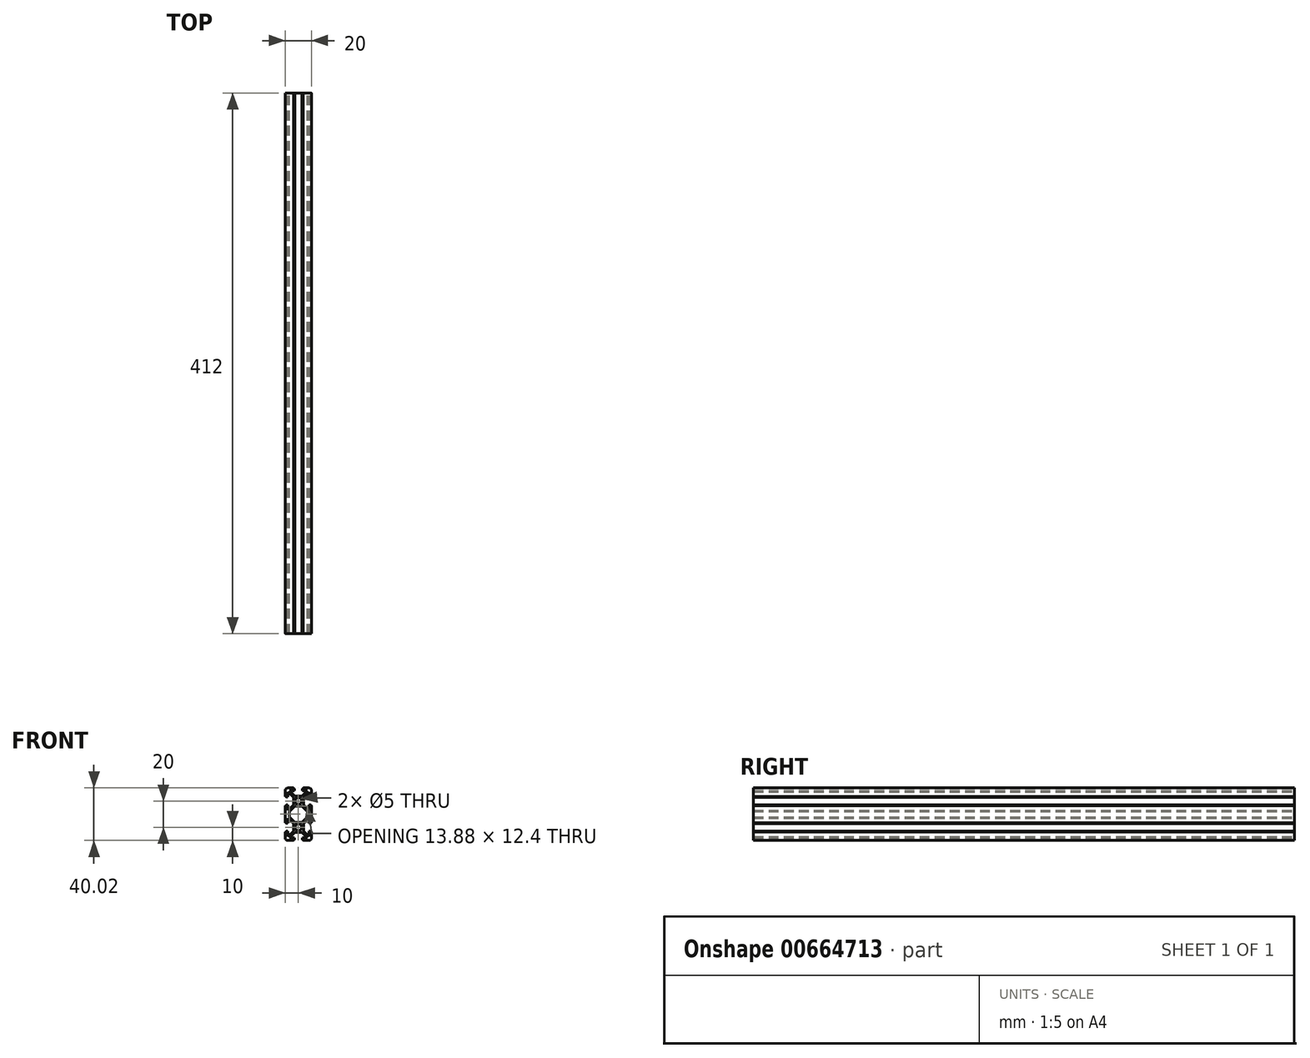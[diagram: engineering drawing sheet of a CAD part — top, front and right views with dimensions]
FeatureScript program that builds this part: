
annotation { "Feature Type Name" : "Feature", "Feature Type Description" : "" }
export const myFeature = defineFeature(function(context is Context, id is Id, definition is map)
    precondition{}
    {
        {
            var Q0;
            Q0=qCreatedBy(makeId("Front.planeOp"),FACE);
            var sketch = newSketch(context, id + "F0", { "sketchPlane" : qUnion([Q0])});
            skPoint(sketch, "E0.middle", {"position": v(10, -10) * mm});
            skPoint(sketch, "E1.visualSharp", {"position": v(0, 0) * mm});
            skArc(sketch, "E1.filletArc", {"start": v(2, 0) * mm, "mid": v(0.59, -0.59) * mm, "end": v(0, -2) * mm});
            skPoint(sketch, "E2.visualSharp", {"position": v(20, 0) * mm});
            skArc(sketch, "E2.filletArc", {"start": v(20, -2) * mm, "mid": v(19.41, -0.59) * mm, "end": v(18, 0) * mm});
            skPoint(sketch, "E3.visualSharp", {"position": v(20, -20) * mm});
            skLineSegment(sketch, "E4", {"start": v(2, 0) * mm, "end": v(6.5, 0) * mm});
            skLineSegment(sketch, "E5", {"start": v(6.5, 0) * mm, "end": v(6.5, -0.5) * mm});
            skLineSegment(sketch, "E6", {"start": v(13.02, -0.5) * mm, "end": v(13.5, -0.5) * mm});
            skLineSegment(sketch, "E7", {"start": v(13.5, 0.02) * mm, "end": v(18, 0) * mm});
            skLineSegment(sketch, "E8", {"start": v(20, -2) * mm, "end": v(20, -6.5) * mm});
            skLineSegment(sketch, "E9", {"start": v(20, -6.5) * mm, "end": v(19.5, -6.5) * mm});
            skLineSegment(sketch, "E10", {"start": v(19.5, -6.5) * mm, "end": v(19.5, -7) * mm});
            skLineSegment(sketch, "E11", {"start": v(13.83, -7.25) * mm, "end": v(13.83, -12.77) * mm});
            skLineSegment(sketch, "E12", {"start": v(19.53, -12.98) * mm, "end": v(19.54, -13.46) * mm});
            skLineSegment(sketch, "E13", {"start": v(12.74, -13.8) * mm, "end": v(7.26, -13.8) * mm});
            skLineSegment(sketch, "E14", {"start": v(6.2, -12.74) * mm, "end": v(6.2, -7.26) * mm});
            skLineSegment(sketch, "E15", {"start": v(0, -6.49) * mm, "end": v(0, -2) * mm});
            skLineSegment(sketch, "E16", {"start": v(7, -0.5) * mm, "end": v(7, -2) * mm});
            skLineSegment(sketch, "E17", {"start": v(7, -2) * mm, "end": v(3.06, -2) * mm});
            skLineSegment(sketch, "E18", {"start": v(3.06, -2) * mm, "end": v(7.26, -6.2) * mm});
            skLineSegment(sketch, "E19", {"start": v(12.74, -6.2) * mm, "end": v(16.94, -2) * mm});
            skLineSegment(sketch, "E20", {"start": v(16.94, -2) * mm, "end": v(13.02, -2) * mm});
            skLineSegment(sketch, "E21", {"start": v(19.53, -12.98) * mm, "end": v(18, -12.98) * mm});
            skLineSegment(sketch, "E22", {"start": v(18, -12.98) * mm, "end": v(18, -16.94) * mm});
            skLineSegment(sketch, "E23", {"start": v(18, -16.94) * mm, "end": v(13.83, -12.77) * mm});
            skLineSegment(sketch, "E24", {"start": v(13.83, -7.25) * mm, "end": v(18, -3.06) * mm});
            skLineSegment(sketch, "E25", {"start": v(18, -3.06) * mm, "end": v(18, -7) * mm});
            skLineSegment(sketch, "E26", {"start": v(18, -7) * mm, "end": v(19.5, -7) * mm});
            skLineSegment(sketch, "E27", {"start": v(16.94, -18) * mm, "end": v(12.74, -13.8) * mm});
            skLineSegment(sketch, "E28", {"start": v(7.26, -13.8) * mm, "end": v(3.06, -18) * mm});
            skLineSegment(sketch, "E29", {"start": v(0.5, -6.49) * mm, "end": v(0.5, -7) * mm});
            skLineSegment(sketch, "E30", {"start": v(0.5, -7) * mm, "end": v(2, -7) * mm});
            skLineSegment(sketch, "E31", {"start": v(2, -7) * mm, "end": v(2, -3.08) * mm});
            skLineSegment(sketch, "E32", {"start": v(2, -3.08) * mm, "end": v(6.2, -7.26) * mm});
            skLineSegment(sketch, "E33", {"start": v(6.2, -12.74) * mm, "end": v(2, -16.94) * mm});
            skLineSegment(sketch, "E34", {"start": v(2, -16.94) * mm, "end": v(2, -13) * mm});
            skLineSegment(sketch, "E35", {"start": v(2, -13) * mm, "end": v(0.5, -13) * mm});
            skLineSegment(sketch, "E36", {"start": v(0.5, -13) * mm, "end": v(0.5, -13.5) * mm});
            skLineSegment(sketch, "E37", {"start": v(0.5, -13.5) * mm, "end": v(0, -13.5) * mm});
            skCircle(sketch, "E38", {"center": v(10, -10) * mm, "radius": 2.5 * mm});
            skLineSegment(sketch, "E39", {"start": v(13.5, 0.02) * mm, "end": v(13.5, -0.5) * mm});
            skLineSegment(sketch, "E40", {"start": v(6.5, -0.5) * mm, "end": v(7, -0.5) * mm});
            skLineSegment(sketch, "E41", {"start": v(13.02, -0.5) * mm, "end": v(13.02, -2) * mm});
            skLineSegment(sketch, "E42", {"start": v(7.26, -6.2) * mm, "end": v(12.74, -6.2) * mm});
            skLineSegment(sketch, "E43", {"start": v(0, -6.49) * mm, "end": v(0.5, -6.49) * mm});
            skLineSegment(sketch, "E44", {"start": v(19.54, -13.46) * mm, "end": v(20, -13.46) * mm});
            skPoint(sketch, "E45.middle", {"position": v(10, -30) * mm});
            skPoint(sketch, "E46.visualSharp", {"position": v(0, -20) * mm});
            skPoint(sketch, "E47.visualSharp", {"position": v(20, -40) * mm});
            skArc(sketch, "E47.filletArc", {"start": v(18, -40) * mm, "mid": v(19.41, -39.41) * mm, "end": v(20, -38) * mm});
            skArc(sketch, "E48.filletArc", {"start": v(0, -38) * mm, "mid": v(0.59, -39.41) * mm, "end": v(2, -40) * mm});
            skLineSegment(sketch, "E49", {"start": v(20, -26.5) * mm, "end": v(19.5, -26.5) * mm});
            skLineSegment(sketch, "E50", {"start": v(19.5, -26.5) * mm, "end": v(19.5, -27) * mm});
            skLineSegment(sketch, "E51", {"start": v(13.83, -27.25) * mm, "end": v(13.83, -32.77) * mm});
            skLineSegment(sketch, "E52", {"start": v(19.53, -32.98) * mm, "end": v(19.54, -33.46) * mm});
            skLineSegment(sketch, "E53", {"start": v(20, -33.46) * mm, "end": v(20, -38) * mm});
            skLineSegment(sketch, "E54", {"start": v(18, -40) * mm, "end": v(13.5, -40) * mm});
            skLineSegment(sketch, "E55", {"start": v(13.5, -40) * mm, "end": v(13.5, -39.5) * mm});
            skLineSegment(sketch, "E56", {"start": v(12.74, -33.8) * mm, "end": v(7.26, -33.8) * mm});
            skLineSegment(sketch, "E57", {"start": v(7, -39.5) * mm, "end": v(6.5, -39.5) * mm});
            skLineSegment(sketch, "E58", {"start": v(6.5, -39.5) * mm, "end": v(6.5, -40) * mm});
            skLineSegment(sketch, "E59", {"start": v(6.5, -40) * mm, "end": v(2, -40) * mm});
            skLineSegment(sketch, "E60", {"start": v(0, -38) * mm, "end": v(0, -33.5) * mm});
            skLineSegment(sketch, "E61", {"start": v(6.2, -32.74) * mm, "end": v(6.2, -27.26) * mm});
            skLineSegment(sketch, "E62", {"start": v(7, -39.5) * mm, "end": v(7, -38) * mm});
            skLineSegment(sketch, "E63", {"start": v(13.02, -39.5) * mm, "end": v(13.02, -38) * mm});
            skLineSegment(sketch, "E64", {"start": v(13.02, -38) * mm, "end": v(16.94, -38) * mm});
            skLineSegment(sketch, "E65", {"start": v(3.06, -22) * mm, "end": v(7.26, -26.2) * mm});
            skLineSegment(sketch, "E66", {"start": v(12.74, -26.2) * mm, "end": v(16.94, -22) * mm});
            skLineSegment(sketch, "E67", {"start": v(19.53, -32.98) * mm, "end": v(18, -32.98) * mm});
            skLineSegment(sketch, "E68", {"start": v(18, -32.98) * mm, "end": v(18, -36.94) * mm});
            skLineSegment(sketch, "E69", {"start": v(18, -36.94) * mm, "end": v(13.83, -32.77) * mm});
            skLineSegment(sketch, "E70", {"start": v(13.83, -27.25) * mm, "end": v(18, -23.06) * mm});
            skLineSegment(sketch, "E71", {"start": v(18, -23.06) * mm, "end": v(18, -27) * mm});
            skLineSegment(sketch, "E72", {"start": v(18, -27) * mm, "end": v(19.5, -27) * mm});
            skLineSegment(sketch, "E73", {"start": v(13.5, -39.5) * mm, "end": v(13.02, -39.5) * mm});
            skLineSegment(sketch, "E74", {"start": v(16.94, -38) * mm, "end": v(12.74, -33.8) * mm});
            skLineSegment(sketch, "E75", {"start": v(7.26, -33.8) * mm, "end": v(3.06, -38) * mm});
            skLineSegment(sketch, "E76", {"start": v(3.06, -38) * mm, "end": v(7, -38) * mm});
            skLineSegment(sketch, "E77", {"start": v(7, -38) * mm, "end": v(7, -39.5) * mm});
            skLineSegment(sketch, "E78", {"start": v(0.5, -26.49) * mm, "end": v(0.5, -27) * mm});
            skLineSegment(sketch, "E79", {"start": v(0.5, -27) * mm, "end": v(2, -27) * mm});
            skLineSegment(sketch, "E80", {"start": v(2, -27) * mm, "end": v(2, -23.08) * mm});
            skLineSegment(sketch, "E81", {"start": v(2, -23.08) * mm, "end": v(6.2, -27.26) * mm});
            skLineSegment(sketch, "E82", {"start": v(6.2, -32.74) * mm, "end": v(2, -36.94) * mm});
            skLineSegment(sketch, "E83", {"start": v(2, -36.94) * mm, "end": v(2, -33) * mm});
            skLineSegment(sketch, "E84", {"start": v(2, -33) * mm, "end": v(0.5, -33) * mm});
            skLineSegment(sketch, "E85", {"start": v(0.5, -33) * mm, "end": v(0.5, -33.5) * mm});
            skLineSegment(sketch, "E86", {"start": v(0.5, -33.5) * mm, "end": v(0, -33.5) * mm});
            skCircle(sketch, "E87", {"center": v(10, -30) * mm, "radius": 2.5 * mm});
            skLineSegment(sketch, "E88", {"start": v(7.26, -26.2) * mm, "end": v(12.74, -26.2) * mm});
            skLineSegment(sketch, "E89", {"start": v(0, -26.49) * mm, "end": v(0.5, -26.49) * mm});
            skLineSegment(sketch, "E90", {"start": v(19.54, -33.46) * mm, "end": v(20, -33.46) * mm});
            skLineSegment(sketch, "E91", {"start": v(0, -13.5) * mm, "end": v(0, -26.49) * mm});
            skLineSegment(sketch, "E92", {"start": v(3.06, -18) * mm, "end": v(3.06, -22) * mm});
            skLineSegment(sketch, "E93", {"start": v(16.94, -18) * mm, "end": v(16.94, -22) * mm});
            skLineSegment(sketch, "E94", {"start": v(20, -13.46) * mm, "end": v(20, -26.5) * mm});
            skSolve(sketch);
        }
        {
            assignVariable(context, id + "F1", {"name" : "L", "anyValue" : 412 * mm});
        }
        {
            var Q0;
            Q0=makeQuery(id+"F0.imprint","IMPRINT",FACE,{"disambiguationData":[TD([[makeQuery(id+"F0.imprint","IMPRINT",EDGE,{"derivedFrom":sQuery(id+"F0.wireOp",EDGE,"E1.filletArc")}),1.0]])]});
            extrude(context, id + "F2", {"entities" : qUnion([Q0]), "depth" : getVariable(context, 'L'), "offsetDistance" : 25 * mm});
        }
    });
